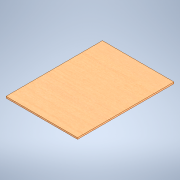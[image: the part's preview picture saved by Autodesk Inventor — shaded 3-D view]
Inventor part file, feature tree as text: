
AUTODESK INVENTOR PART (.ipt)
format: ipt  version: 2021 (Build 250183000, 183)  size: 102,912 bytes
history: native  units: mm
features: extrude x1, sketch x1
ambient origin geometry x8: Origin, YZ Plane, XZ Plane, XY Plane, X Axis, Y Axis, Z Axis, Center Point
bodies: Solid1 (feature_tree)
feature tree (2):
  extrude  "Extrusion1"  Depth=194.0mm
  sketch  "Sketch1"  dims[d0=144.0mm d1=194.0mm d2=3.0mm d3=0.0mm]
